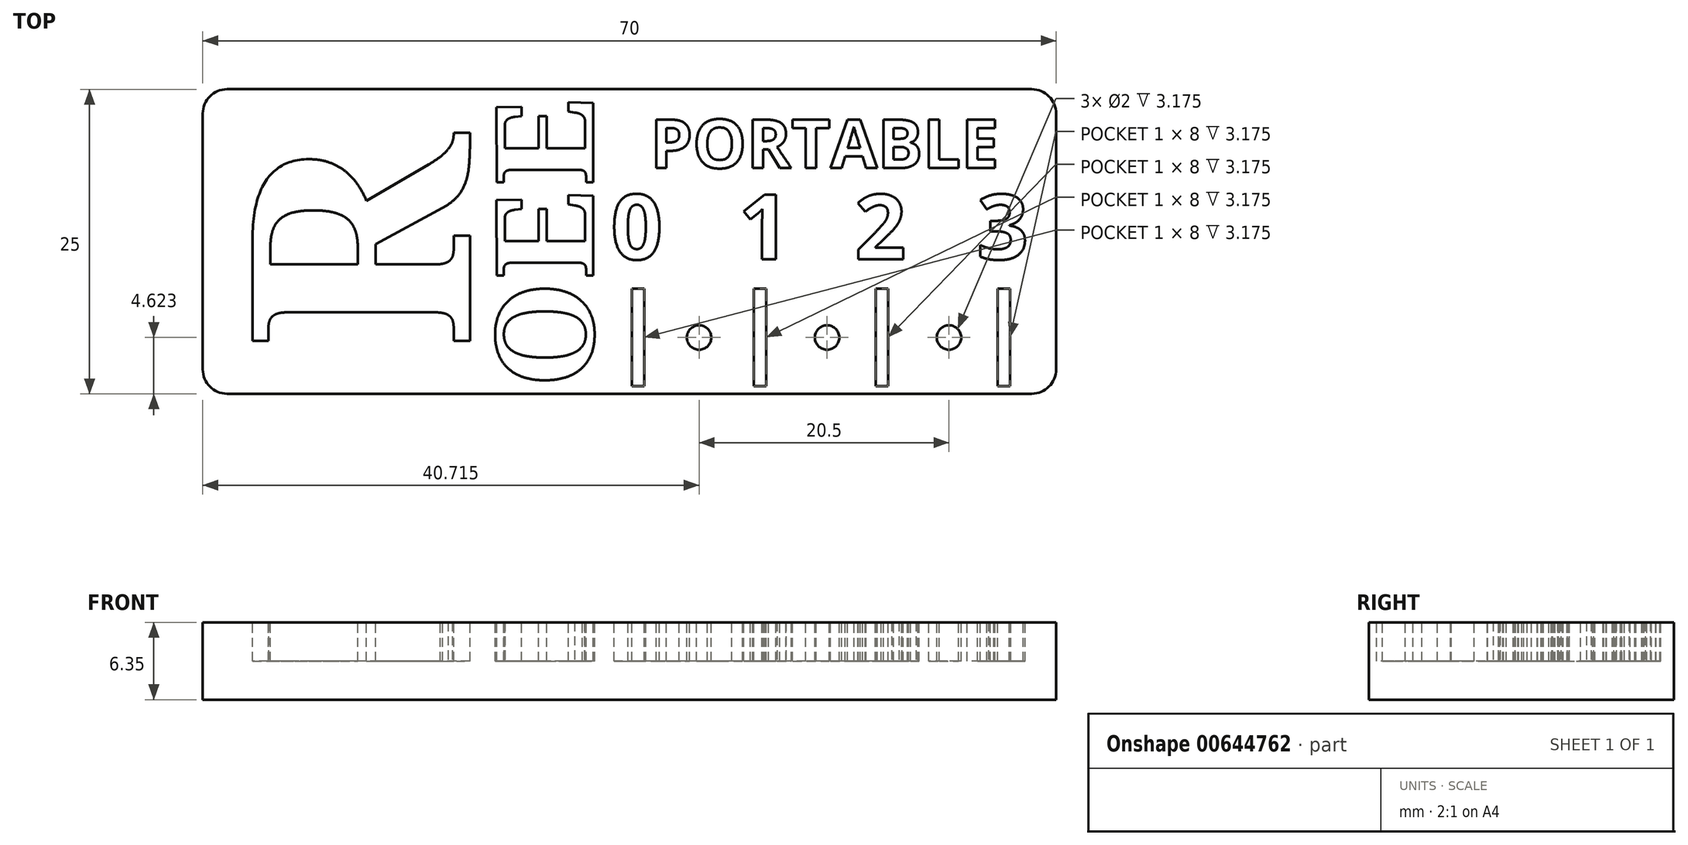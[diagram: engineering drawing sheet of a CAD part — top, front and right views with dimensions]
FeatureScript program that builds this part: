
annotation { "Feature Type Name" : "Feature", "Feature Type Description" : "" }
export const myFeature = defineFeature(function(context is Context, id is Id, definition is map)
    precondition{}
    {
        {
            var Q0;
            Q0=qCreatedBy(makeId("Top.planeOp"),FACE);
            var sketch = newSketch(context, id + "F0", { "sketchPlane" : qUnion([Q0])});
            skLineSegment(sketch, "E0.bottom", {"start": v(-55.27, 9.73) * mm, "end": v(10.73, 9.73) * mm});
            skLineSegment(sketch, "E0.top", {"start": v(-55.27, -15.27) * mm, "end": v(10.73, -15.27) * mm});
            skLineSegment(sketch, "E0.left", {"start": v(-57.27, 7.73) * mm, "end": v(-57.27, -13.27) * mm});
            skLineSegment(sketch, "E0.right", {"start": v(12.73, 7.73) * mm, "end": v(12.73, -13.27) * mm});
            skPoint(sketch, "E1.visualSharp", {"position": v(-57.27, 9.73) * mm});
            skArc(sketch, "E1.filletArc", {"start": v(-55.27, 9.73) * mm, "mid": v(-56.68, 9.15) * mm, "end": v(-57.27, 7.73) * mm});
            skPoint(sketch, "E2.visualSharp", {"position": v(12.73, 9.73) * mm});
            skArc(sketch, "E2.filletArc", {"start": v(12.73, 7.73) * mm, "mid": v(12.14, 9.15) * mm, "end": v(10.73, 9.73) * mm});
            skPoint(sketch, "E3.visualSharp", {"position": v(12.73, -15.27) * mm});
            skArc(sketch, "E3.filletArc", {"start": v(10.73, -15.27) * mm, "mid": v(12.14, -14.68) * mm, "end": v(12.73, -13.27) * mm});
            skPoint(sketch, "E4.visualSharp", {"position": v(-57.27, -15.27) * mm});
            skArc(sketch, "E4.filletArc", {"start": v(-57.27, -13.27) * mm, "mid": v(-56.68, -14.68) * mm, "end": v(-55.27, -15.27) * mm});
            skSolve(sketch);
        }
        {
            var Q0;
            Q0=qSketchRegion(id+"F0",true);
            extrude(context, id + "F1", {"entities" : qUnion([Q0]), "depth" : 6.35 * mm, "offsetDistance" : 25.4 * mm});
        }
        {
            var Q0;
            Q0=makeQuery(id+"F1.opExtrude","CAP_FACE",FACE,{"disambiguationData":[OSD([sQuery(id+"F0.wireOp",EDGE,"E0.bottom"),sQuery(id+"F0.wireOp",EDGE,"E0.top"),sQuery(id+"F0.wireOp",EDGE,"E0.left"),sQuery(id+"F0.wireOp",EDGE,"E0.right")])],"isStart":false});
            var sketch = newSketch(context, id + "F2", { "sketchPlane" : qUnion([Q0])});
            skText(sketch, "E5", { "text": "R", "fontName": "NotoSerif-Bold.ttf"});
            skText(sketch, "E6", { "text": "O\n", "fontName": "NotoSerif-Bold.ttf"});
            skText(sketch, "E7", { "text": "E", "fontName": "NotoSerif-Bold.ttf"});
            skLineSegment(sketch, "E8.bottom", {"start": v(-22.06, -6.65) * mm, "end": v(-21.06, -6.65) * mm});
            skLineSegment(sketch, "E8.top", {"start": v(-22.06, -14.65) * mm, "end": v(-21.06, -14.65) * mm});
            skLineSegment(sketch, "E8.left", {"start": v(-22.06, -6.65) * mm, "end": v(-22.06, -14.65) * mm});
            skLineSegment(sketch, "E8.right", {"start": v(-21.06, -6.65) * mm, "end": v(-21.06, -14.65) * mm});
            skLineSegment(sketch, "E9.bottom", {"start": v(-12.06, -6.65) * mm, "end": v(-11.06, -6.65) * mm});
            skLineSegment(sketch, "E9.top", {"start": v(-12.06, -14.65) * mm, "end": v(-11.06, -14.65) * mm});
            skLineSegment(sketch, "E9.left", {"start": v(-12.06, -6.65) * mm, "end": v(-12.06, -14.65) * mm});
            skLineSegment(sketch, "E9.right", {"start": v(-11.06, -6.65) * mm, "end": v(-11.06, -14.65) * mm});
            skLineSegment(sketch, "E10.bottom", {"start": v(-2.06, -6.65) * mm, "end": v(-1.06, -6.65) * mm});
            skLineSegment(sketch, "E10.top", {"start": v(-2.06, -14.65) * mm, "end": v(-1.06, -14.65) * mm});
            skLineSegment(sketch, "E10.left", {"start": v(-2.06, -6.65) * mm, "end": v(-2.06, -14.65) * mm});
            skLineSegment(sketch, "E10.right", {"start": v(-1.06, -6.65) * mm, "end": v(-1.06, -14.65) * mm});
            skLineSegment(sketch, "E11.bottom", {"start": v(7.94, -6.65) * mm, "end": v(8.94, -6.65) * mm});
            skLineSegment(sketch, "E11.top", {"start": v(7.94, -14.65) * mm, "end": v(8.94, -14.65) * mm});
            skLineSegment(sketch, "E11.left", {"start": v(7.94, -6.65) * mm, "end": v(7.94, -14.65) * mm});
            skLineSegment(sketch, "E11.right", {"start": v(8.94, -6.65) * mm, "end": v(8.94, -14.65) * mm});
            skPoint(sketch, "E12", {"position": v(-21.56, -6.65) * mm});
            skPoint(sketch, "E13", {"position": v(-11.56, -6.65) * mm});
            skPoint(sketch, "E14", {"position": v(-1.56, -6.65) * mm});
            skCircle(sketch, "E15", {"center": v(-16.56, -10.65) * mm, "radius": 1 * mm});
            skPoint(sketch, "E16", {"position": v(-21.06, -10.65) * mm});
            skCircle(sketch, "E17", {"center": v(-6.06, -10.65) * mm, "radius": 1 * mm});
            skCircle(sketch, "E18", {"center": v(3.94, -10.65) * mm, "radius": 1 * mm});
            skPoint(sketch, "E19", {"position": v(-11.06, -10.65) * mm});
            skPoint(sketch, "E20", {"position": v(-1.06, -10.65) * mm});
            skText(sketch, "E21", { "text": "0", "fontName": "OpenSans-Bold.ttf"});
            skText(sketch, "E22", { "text": "1", "fontName": "OpenSans-Bold.ttf"});
            skText(sketch, "E23", { "text": "2", "fontName": "OpenSans-Bold.ttf"});
            skText(sketch, "E24", { "text": "3", "fontName": "OpenSans-Bold.ttf"});
            skLineSegment(sketch, "E25", {"start": v(-39.23, 23.36) * mm, "end": v(-48.9, 23.36) * mm});
            skLineSegment(sketch, "E26", {"start": v(-48.9, 23.36) * mm, "end": v(-48.9, 20.36) * mm});
            skLineSegment(sketch, "E27", {"start": v(-48.9, 20.36) * mm, "end": v(-53.2, 24.99) * mm});
            skLineSegment(sketch, "E28", {"start": v(-53.2, 24.99) * mm, "end": v(-48.9, 28.97) * mm});
            skLineSegment(sketch, "E29", {"start": v(-48.9, 28.97) * mm, "end": v(-48.9, 25.97) * mm});
            skLineSegment(sketch, "E30", {"start": v(-48.9, 25.97) * mm, "end": v(-39.23, 25.97) * mm});
            skPoint(sketch, "E31", {"position": v(-41.72, 24.66) * mm});
            skLineSegment(sketch, "E32", {"start": v(-41.72, 24.66) * mm, "end": v(-39.23, 23.36) * mm});
            skLineSegment(sketch, "E33", {"start": v(-41.72, 24.66) * mm, "end": v(-39.23, 25.97) * mm});
            skText(sketch, "E34", { "text": "E", "fontName": "NotoSerif-Bold.ttf"});
            skText(sketch, "E35", { "text": "PORTABLE", "fontName": "OpenSans-Bold.ttf"});
            const initialGuessF2  = {"E5": [-0.03535, -0.01161, 0, 1, 0.018], "E6": [-0.02523, -0.01477, 0, 1, 0.008], "E7": [-0.02523, -0.00585, -0.00042, 1, 0.008], "E21": [-0.02378, -0.00422, 1, 0, 0.00534], "E22": [-0.01333, -0.00422, 1, 0, 0.00534], "E23": [-0.0038, -0.00422, 1, 0, 0.00534], "E24": [0.00623, -0.00422, 1, 0, 0.00534], "E34": [-0.02523, 0.00178, -0.00042, 1, 0.008], "E35": [-0.02057, 0.00327, 1, 0, 0.004]};
            skSetInitialGuess(sketch, initialGuessF2);
            skSolve(sketch);
        }
        {
            var Q0;
            Q0=qSketchRegion(id+"F2",true);
            extrude(context, id + "F3", {"entities" : qUnion([Q0]), "operationType" : NewBodyOperationType.REMOVE, "oppositeDirection" : true, "depth" : 3.17 * mm, "offsetDistance" : 25.4 * mm});
        }
    });
